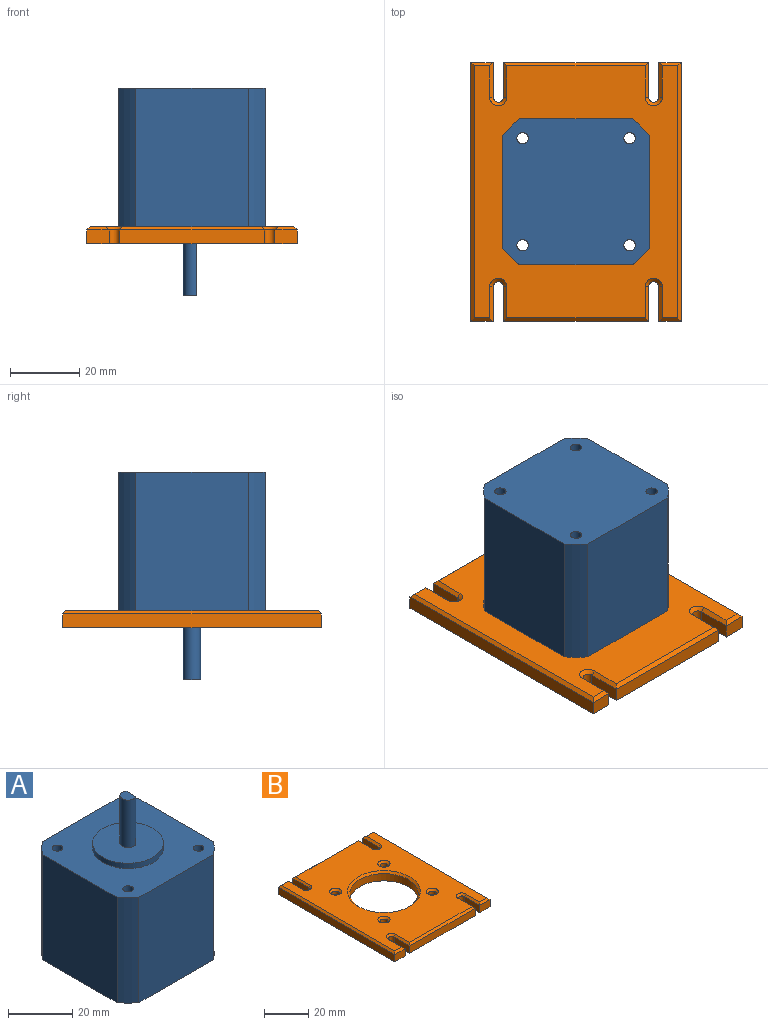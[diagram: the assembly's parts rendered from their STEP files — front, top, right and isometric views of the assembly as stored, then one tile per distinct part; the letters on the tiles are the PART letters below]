
ASSEMBLY  parts=2 mates=1
PART A: 19 faces, bbox 42.3x42.3x60 mm
  f0: plane 22x22mm, normal (0,0,1), area 364.3mm2, adj f15,f16,f17
  f1: plane 40x32.67mm, normal (0,1,0), area 1307mm2, adj f2,f12,f13,f14
  f2: cylinder r=26.72mm len=40mm, axis (0,0,-1), area 273mm2, adj f1,f3,f13,f14
  f3: plane 40x32.67mm, normal (-1,0,0), area 1307mm2, adj f2,f4,f13,f14
  f4: cylinder r=26.72mm len=40mm, axis (0,0,-1), area 273mm2, adj f3,f5,f13,f14
  f5: plane 40x32.67mm, normal (0,-1,0), area 1307mm2, adj f4,f6,f13,f14
  f6: cylinder r=26.72mm len=40mm, axis (0,0,-1), area 273mm2, adj f5,f7,f13,f14
  f7: plane 40x32.67mm, normal (1,0,0), area 1307mm2, adj f6,f12,f13,f14
  f8: cylinder r=1.65mm len=40mm, axis (0,0,-1), area 414.7mm2, adj f13,f14
  f9: cylinder r=1.65mm len=40mm, axis (0,0,-1), area 414.7mm2, adj f13,f14
  f10: cylinder r=1.65mm len=40mm, axis (0,0,-1), area 414.7mm2, adj f13,f14
  f11: cylinder r=1.65mm len=40mm, axis (0,0,-1), area 414.7mm2, adj f13,f14
  f12: cylinder r=26.72mm len=40mm, axis (0,0,-1), area 273mm2, adj f1,f7,f13,f14
  f13: plane 42.3x42.3mm, normal (0,0,1), area 1332.6mm2, adj f1,f2,f3,f4,f5,f6,f7,f8
  f14: plane 42.3x42.3mm, normal (0,0,-1), area 1712.7mm2, adj f1,f2,f3,f4,f5,f6,f7,f8
  f15: cylinder r=11mm len=22mm, axis (0,0,-1), area 138.2mm2, adj f0,f13
  f16: plane 18x4.33mm, normal (1,0,0), area 77.9mm2, adj f0,f17,f18
  f17: cylinder r=2.5mm len=18mm, axis (0,0,-1), area 188.5mm2, adj f0,f16,f18
  f18: plane 5x3.75mm, normal (0,0,1), area 15.8mm2, adj f16,f17
PART B: 56 faces, bbox 61x75x5 mm
  f0: cylinder r=1.5mm len=4mm, axis (0,0,-1), area 18.8mm2, adj f1,f20,f22,f38
  f1: plane 10x4mm, normal (1,0,0), area 40mm2, adj f0,f2,f22,f40
  f2: plane 42x4mm, normal (0,1,0), area 168mm2, adj f1,f3,f22,f42
  f3: plane 10x4mm, normal (-1,0,0), area 40mm2, adj f2,f4,f22,f44
  f4: cylinder r=1.5mm len=4mm, axis (0,0,-1), area 18.8mm2, adj f3,f5,f22,f46
  f5: plane 10x4mm, normal (1,0,0), area 40mm2, adj f4,f6,f22,f48
  f6: plane 6.5x4mm, normal (0,1,0), area 26mm2, adj f5,f7,f22,f50
  f7: plane 75x4mm, normal (-1,0,0), area 300mm2, adj f6,f8,f22,f52
  f8: plane 6.5x4mm, normal (0,-1,0), area 26mm2, adj f7,f9,f22,f54
  f9: plane 10x4mm, normal (1,0,0), area 40mm2, adj f8,f10,f22,f55
  f10: cylinder r=1.5mm len=4mm, axis (0,0,-1), area 18.8mm2, adj f9,f11,f22,f53
  f11: plane 10x4mm, normal (-1,0,0), area 40mm2, adj f10,f12,f22,f51
  f12: plane 42x4mm, normal (0,-1,0), area 168mm2, adj f11,f13,f22,f49
  f13: plane 10x4mm, normal (1,0,0), area 40mm2, adj f12,f14,f22,f47
  f14: cylinder r=1.5mm len=4mm, axis (0,0,-1), area 18.8mm2, adj f13,f15,f22,f45
  f15: plane 10x4mm, normal (-1,0,0), area 40mm2, adj f14,f16,f22,f43
  f16: plane 6.5x4mm, normal (0,-1,0), area 26mm2, adj f15,f17,f22,f41
  f17: plane 75x4mm, normal (1,0,0), area 300mm2, adj f16,f18,f22,f39
  f18: plane 6.5x4mm, normal (0,1,0), area 26mm2, adj f17,f20,f22,f37
  f19: cylinder r=15.5mm len=31mm, axis (0,0,-1), area 389.6mm2, adj f22,f35
  f20: plane 10x4mm, normal (-1,0,0), area 40mm2, adj f0,f18,f22,f36
  f21: plane 73x59mm, normal (0,0,1), area 3137.4mm2, adj f31,f32,f33,f34,f35,f36,f37,f38
  f22: plane 75x61mm, normal (0,0,-1), area 3509.4mm2, adj f0,f1,f2,f3,f4,f5,f6,f7
  f23: cylinder r=1.75mm len=3.5mm, axis (0,0,-1), area 22mm2, adj f24,f34
  f24: cone r=1.75mm half-angle=45deg, axis (0,0,-1), area 48.9mm2, adj f22,f23
  f25: cylinder r=1.75mm len=3.5mm, axis (0,0,-1), area 22mm2, adj f26,f33
  f26: cone r=1.75mm half-angle=45deg, axis (0,0,-1), area 48.9mm2, adj f22,f25
  f27: cylinder r=1.75mm len=3.5mm, axis (0,0,-1), area 22mm2, adj f28,f32
  f28: cone r=1.75mm half-angle=45deg, axis (0,0,-1), area 48.9mm2, adj f22,f27
  f29: cylinder r=1.75mm len=3.5mm, axis (0,0,-1), area 22mm2, adj f30,f31
  f30: cone r=1.75mm half-angle=45deg, axis (0,0,-1), area 48.9mm2, adj f22,f29
  f31: cone r=2.75mm half-angle=45deg, axis (0,0,1), area 20mm2, adj f21,f29
  f32: cone r=2.75mm half-angle=45deg, axis (0,0,1), area 20mm2, adj f21,f27
  f33: cone r=2.75mm half-angle=45deg, axis (0,0,1), area 20mm2, adj f21,f25
  f34: cone r=2.75mm half-angle=45deg, axis (0,0,1), area 20mm2, adj f21,f23
  f35: cone r=15.5mm half-angle=45deg, axis (0,0,1), area 142.2mm2, adj f19,f21
  f36: plane 10x1mm, normal (-0.71,0,0.71), area 13.4mm2, adj f20,f21,f37,f38
  f37: plane 6.5x1mm, normal (0,0.71,0.71), area 7.8mm2, adj f18,f21,f36,f39
  f38: cone r=2.5mm half-angle=45deg, axis (0,0,1), area 8.9mm2, adj f0,f21,f36,f40
  f39: plane 75x1mm, normal (0.71,0,0.71), area 104.7mm2, adj f17,f21,f37,f41
  f40: plane 10x1mm, normal (0.71,0,0.71), area 13.4mm2, adj f1,f21,f38,f42
  f41: plane 6.5x1mm, normal (0,-0.71,0.71), area 7.8mm2, adj f16,f21,f39,f43
  f42: plane 42x1mm, normal (0,0.71,0.71), area 58mm2, adj f2,f21,f40,f44
  f43: plane 10x1mm, normal (-0.71,0,0.71), area 13.4mm2, adj f15,f21,f41,f45
  f44: plane 10x1mm, normal (-0.71,0,0.71), area 13.4mm2, adj f3,f21,f42,f46
  f45: cone r=1.5mm half-angle=45deg, axis (0,0,1), area 8.9mm2, adj f14,f21,f43,f47
  f46: cone r=2.5mm half-angle=45deg, axis (0,0,1), area 8.9mm2, adj f4,f21,f44,f48
  f47: plane 10x1mm, normal (0.71,0,0.71), area 13.4mm2, adj f13,f21,f45,f49
  f48: plane 10x1mm, normal (0.71,0,0.71), area 13.4mm2, adj f5,f21,f46,f50
  f49: plane 42x1mm, normal (0,-0.71,0.71), area 58mm2, adj f12,f21,f47,f51
  f50: plane 6.5x1mm, normal (0,0.71,0.71), area 7.8mm2, adj f6,f21,f48,f52
  f51: plane 10x1mm, normal (-0.71,0,0.71), area 13.4mm2, adj f11,f21,f49,f53
  f52: plane 75x1mm, normal (-0.71,0,0.71), area 104.7mm2, adj f7,f21,f50,f54
  f53: cone r=1.5mm half-angle=45deg, axis (0,0,1), area 8.9mm2, adj f10,f21,f51,f55
  f54: plane 6.5x1mm, normal (0,-0.71,0.71), area 7.8mm2, adj f8,f21,f52,f55
  f55: plane 10x1mm, normal (0.71,0,0.71), area 13.4mm2, adj f9,f21,f53,f54
PLACE A rot(axis=(1,0,0),180deg) t=(0,0,45)mm
PLACE B at identity
MATE fastened A.f15 <-> B.f19  axis (0,0,-1) through (0,0,5)mm
